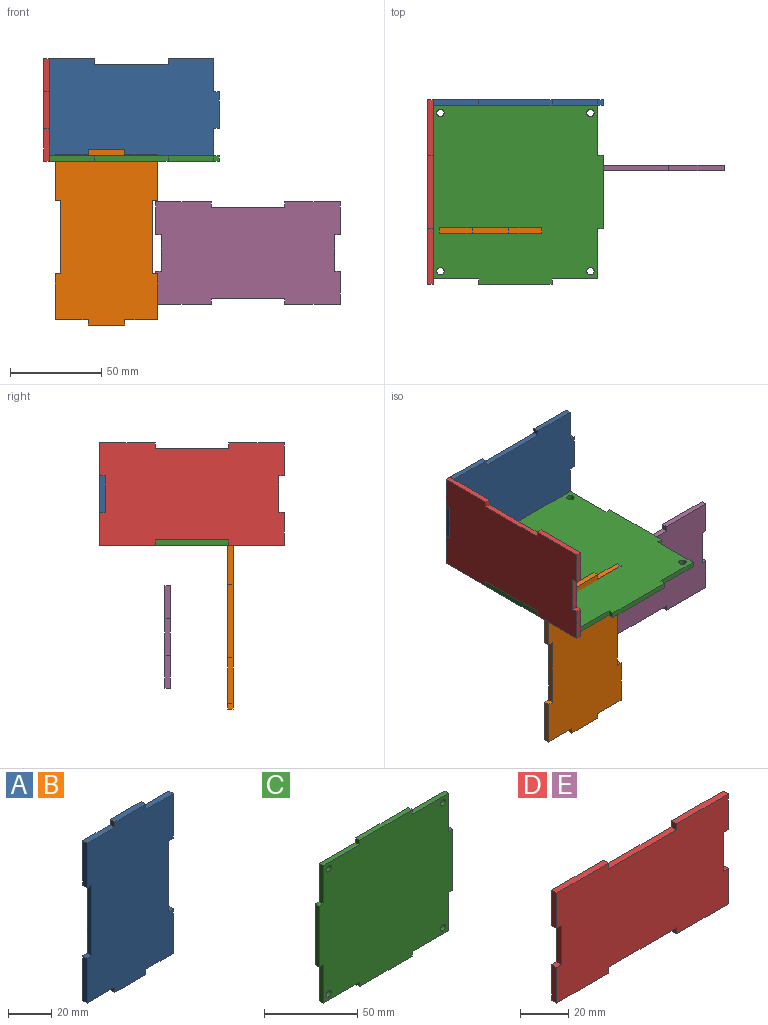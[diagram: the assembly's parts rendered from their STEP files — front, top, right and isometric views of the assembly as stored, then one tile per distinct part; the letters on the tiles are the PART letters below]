
ASSEMBLY  parts=5 mates=2
PART A: 22 faces, bbox 56x3x96 mm
  f0: plane 3x3mm, normal (1,0,0), area 9mm2, adj f1,f19,f20,f21
  f1: plane 18x3mm, normal (0,0,-1), area 54mm2, adj f0,f2,f20,f21
  f2: plane 25x3mm, normal (1,0,0), area 75mm2, adj f1,f3,f20,f21
  f3: plane 3x3mm, normal (0,0,1), area 9mm2, adj f2,f4,f20,f21
  f4: plane 40x3mm, normal (1,0,0), area 120mm2, adj f3,f5,f20,f21
  f5: plane 3x3mm, normal (0,0,-1), area 9mm2, adj f4,f6,f20,f21
  f6: plane 25x3mm, normal (1,0,0), area 75mm2, adj f5,f7,f20,f21
  f7: plane 18x3mm, normal (0,0,1), area 54mm2, adj f6,f8,f20,f21
  f8: plane 3x3mm, normal (1,0,0), area 9mm2, adj f7,f9,f20,f21
  f9: plane 20x3mm, normal (0,0,1), area 60mm2, adj f8,f10,f20,f21
  f10: plane 3x3mm, normal (-1,0,0), area 9mm2, adj f9,f11,f20,f21
  f11: plane 18x3mm, normal (0,0,1), area 54mm2, adj f10,f12,f20,f21
  f12: plane 25x3mm, normal (-1,0,0), area 75mm2, adj f11,f13,f20,f21
  f13: plane 3x3mm, normal (0,0,-1), area 9mm2, adj f12,f14,f20,f21
  f14: plane 40x3mm, normal (-1,0,0), area 120mm2, adj f13,f15,f20,f21
  f15: plane 3x3mm, normal (0,0,1), area 9mm2, adj f14,f16,f20,f21
  f16: plane 25x3mm, normal (-1,0,0), area 75mm2, adj f15,f17,f20,f21
  f17: plane 18x3mm, normal (0,0,-1), area 54mm2, adj f16,f18,f20,f21
  f18: plane 3x3mm, normal (-1,0,0), area 9mm2, adj f17,f19,f20,f21
  f19: plane 20x3mm, normal (0,0,-1), area 60mm2, adj f0,f18,f20,f21
  f20: plane 96x56mm, normal (0,-1,0), area 4920mm2, adj f0,f1,f2,f3,f4,f5,f6,f7
  f21: plane 96x56mm, normal (0,1,0), area 4920mm2, adj f0,f1,f2,f3,f4,f5,f6,f7
PART B: same geometry as A
PART C: 26 faces, bbox 101x3x96 mm
  f0: plane 25x3mm, normal (1,0,0), area 75mm2, adj f1,f19,f24,f25
  f1: plane 3x3mm, normal (0,0,-1), area 9mm2, adj f0,f2,f24,f25
  f2: plane 40x3mm, normal (1,0,0), area 120mm2, adj f1,f3,f24,f25
  f3: plane 3x3mm, normal (0,0,1), area 9mm2, adj f2,f4,f24,f25
  f4: plane 25x3mm, normal (1,0,0), area 75mm2, adj f3,f5,f24,f25
  f5: plane 27.5x3mm, normal (0,0,1), area 82.5mm2, adj f4,f6,f24,f25
  f6: plane 3x3mm, normal (1,0,0), area 9mm2, adj f5,f7,f24,f25
  f7: plane 40x3mm, normal (0,0,1), area 120mm2, adj f6,f8,f24,f25
  f8: plane 3x3mm, normal (-1,0,0), area 9mm2, adj f7,f9,f24,f25
  f9: plane 27.5x3mm, normal (0,0,1), area 82.5mm2, adj f8,f10,f24,f25
  f10: plane 25x3mm, normal (-1,0,0), area 75mm2, adj f9,f11,f24,f25
  f11: plane 3x3mm, normal (0,0,1), area 9mm2, adj f10,f12,f24,f25
  f12: plane 40x3mm, normal (-1,0,0), area 120mm2, adj f11,f13,f24,f25
  f13: plane 3x3mm, normal (0,0,-1), area 9mm2, adj f12,f14,f24,f25
  f14: plane 25x3mm, normal (-1,0,0), area 75mm2, adj f13,f15,f24,f25
  f15: plane 27.5x3mm, normal (0,0,-1), area 82.5mm2, adj f14,f16,f24,f25
  f16: plane 3x3mm, normal (-1,0,0), area 9mm2, adj f15,f17,f24,f25
  f17: plane 40x3mm, normal (0,0,-1), area 120mm2, adj f16,f18,f24,f25
  f18: plane 3x3mm, normal (1,0,0), area 9mm2, adj f17,f19,f24,f25
  f19: plane 27.5x3mm, normal (0,0,-1), area 82.5mm2, adj f0,f18,f24,f25
  f20: cylinder r=2mm len=4mm, axis (0,1,0), area 37.7mm2, adj f24,f25
  f21: cylinder r=2mm len=4mm, axis (0,1,0), area 37.7mm2, adj f24,f25
  f22: cylinder r=2mm len=4mm, axis (0,1,0), area 37.7mm2, adj f24,f25
  f23: cylinder r=2mm len=4mm, axis (0,1,0), area 37.7mm2, adj f24,f25
  f24: plane 101x96mm, normal (0,-1,0), area 8979.7mm2, adj f0,f1,f2,f3,f4,f5,f6,f7
  f25: plane 101x96mm, normal (0,1,0), area 8979.7mm2, adj f0,f1,f2,f3,f4,f5,f6,f7
PART D: 22 faces, bbox 101x3x56 mm
  f0: plane 3x3mm, normal (-1,0,0), area 9mm2, adj f1,f19,f20,f21
  f1: plane 30.5x3mm, normal (0,0,-1), area 91.5mm2, adj f0,f2,f20,f21
  f2: plane 18x3mm, normal (1,0,0), area 54mm2, adj f1,f3,f20,f21
  f3: plane 3x3mm, normal (0,0,1), area 9mm2, adj f2,f4,f20,f21
  f4: plane 20x3mm, normal (1,0,0), area 60mm2, adj f3,f5,f20,f21
  f5: plane 3x3mm, normal (0,0,-1), area 9mm2, adj f4,f6,f20,f21
  f6: plane 18x3mm, normal (1,0,0), area 54mm2, adj f5,f7,f20,f21
  f7: plane 30.5x3mm, normal (0,0,1), area 91.5mm2, adj f6,f8,f20,f21
  f8: plane 3x3mm, normal (-1,0,0), area 9mm2, adj f7,f9,f20,f21
  f9: plane 40x3mm, normal (0,0,1), area 120mm2, adj f8,f10,f20,f21
  f10: plane 3x3mm, normal (1,0,0), area 9mm2, adj f9,f11,f20,f21
  f11: plane 30.5x3mm, normal (0,0,1), area 91.5mm2, adj f10,f12,f20,f21
  f12: plane 18x3mm, normal (-1,0,0), area 54mm2, adj f11,f13,f20,f21
  f13: plane 3x3mm, normal (0,0,-1), area 9mm2, adj f12,f14,f20,f21
  f14: plane 20x3mm, normal (-1,0,0), area 60mm2, adj f13,f15,f20,f21
  f15: plane 3x3mm, normal (0,0,1), area 9mm2, adj f14,f16,f20,f21
  f16: plane 18x3mm, normal (-1,0,0), area 54mm2, adj f15,f17,f20,f21
  f17: plane 30.5x3mm, normal (0,0,-1), area 91.5mm2, adj f16,f18,f20,f21
  f18: plane 3x3mm, normal (1,0,0), area 9mm2, adj f17,f19,f20,f21
  f19: plane 40x3mm, normal (0,0,-1), area 120mm2, adj f0,f18,f20,f21
  f20: plane 101x56mm, normal (0,-1,0), area 5296mm2, adj f0,f1,f2,f3,f4,f5,f6,f7
  f21: plane 101x56mm, normal (0,1,0), area 5296mm2, adj f0,f1,f2,f3,f4,f5,f6,f7
PART E: same geometry as D
PLACE A rot(axis=(0.71,0,0.71),180deg) t=(3.69,44.94,42.87)mm
PLACE B t=(-9.97,-22,-26.62)mm
PLACE C rot(axis=(0.58,-0.58,-0.58),120deg) t=(3.69,-2.56,17.87)mm
PLACE D rot(axis=(0,0,-1),90deg) t=(-41.31,-2.56,42.87)mm
PLACE E t=(67.43,12.21,-35.27)mm
MATE fastened C.f13 <-> A.f13  axis (1,0,0) through (23.69,46.44,16.37)mm
MATE fastened D.f0 <-> C.f6  axis (0,1,0) through (-42.81,-22.56,16.37)mm
